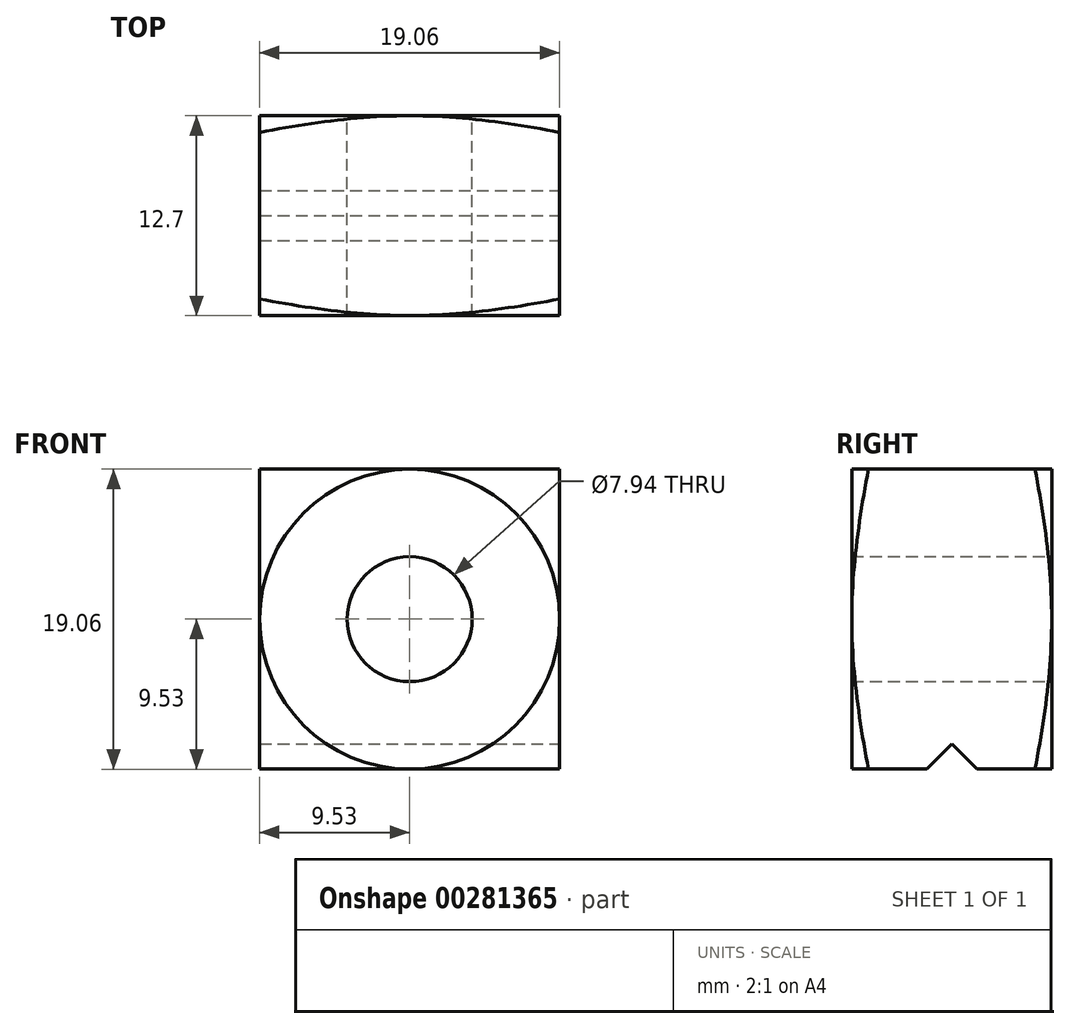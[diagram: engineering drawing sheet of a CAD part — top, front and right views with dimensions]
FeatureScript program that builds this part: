
annotation { "Feature Type Name" : "Feature", "Feature Type Description" : "" }
export const myFeature = defineFeature(function(context is Context, id is Id, definition is map)
    precondition{}
    {
        {
            var Q0;
            Q0=qCreatedBy(makeId("Front.planeOp"),FACE);
            var sketch = newSketch(context, id + "F0", { "sketchPlane" : qUnion([Q0])});
            skLineSegment(sketch, "E0.bottom", {"start": v(-9.52, -9.52) * mm, "end": v(9.52, -9.52) * mm});
            skLineSegment(sketch, "E0.top", {"start": v(-9.53, 9.52) * mm, "end": v(9.53, 9.52) * mm});
            skLineSegment(sketch, "E0.left", {"start": v(-9.53, -9.52) * mm, "end": v(-9.53, 9.52) * mm});
            skLineSegment(sketch, "E0.right", {"start": v(9.53, -9.52) * mm, "end": v(9.53, 9.52) * mm});
            skPoint(sketch, "E0.middle", {"position": v(0, 0) * mm});
            skCircle(sketch, "E1", {"center": v(0, 0) * mm, "radius": 3.97 * mm});
            skCircle(sketch, "E2", {"center": v(0, 0) * mm, "radius": 9.53 * mm});
            skSolve(sketch);
        }
        {
            var Q0;
            Q0=qSketchRegion(id+"F0",true);
            extrude(context, id + "F1", {"entities" : qUnion([Q0]), "depth" : 12.7 * mm});
        }
        {
            var Q0;
            Q0=makeQuery(id+"F1.opExtrude","SWEPT_FACE",FACE,{"disambiguationData":[OSD([sQuery(id+"F0.wireOp",EDGE,"E0.right")])]});
            var sketch = newSketch(context, id + "F2", { "sketchPlane" : qUnion([Q0])});
            skLineSegment(sketch, "E3", {"start": v(-6.35, -7.94) * mm, "end": v(-7.94, -9.52) * mm});
            skPoint(sketch, "E3.startSnap0", {"position": v(-6.35, -9.52) * mm});
            skLineSegment(sketch, "E4", {"start": v(-6.35, -7.94) * mm, "end": v(-4.76, -9.52) * mm});
            skLineSegment(sketch, "E5", {"start": v(-6.35, -7.94) * mm, "end": v(-6.35, -15.34) * mm, "construction": true});
            skSolve(sketch);
        }
        {
            var Q0;
            Q0=qSketchRegion(id+"F2",true);
            var Q1;
            {var subQ0=sQuery(id+"F2.wireOp",EDGE,"E3");Q1=makeQuery(id+"F2.imprint","IMPRINT",FACE,{"disambiguationData":[TD([[makeQuery(id+"F2.imprint","IMPRINT",EDGE,{"derivedFrom":subQ0}),1.0]])]});}
            extrude(context, id + "F3", {"entities" : qUnion([Q0, Q1]), "operationType" : NewBodyOperationType.REMOVE, "oppositeDirection" : true, "depth" : 19.05 * mm});
        }
        {
            var Q0;
            Q0=makeQuery(id+"F1.opExtrude","SWEPT_FACE",FACE,{"disambiguationData":[OSD([sQuery(id+"F0.wireOp",EDGE,"E0.right")])]});
            var Q1;
            Q1=makeQuery(id+"F1.opExtrude","SWEPT_FACE",FACE,{"disambiguationData":[OSD([sQuery(id+"F0.wireOp",EDGE,"E0.left")])]});
            cPlane(context, id + "F4", {"entities" : qUnion([Q0, Q1]), "cplaneType" : CPlaneType.MID_PLANE, "offset" : 25.4 * mm, "width" : 152.4 * mm, "height" : 152.4 * mm});
        }
        {
            var Q0;
            Q0=qCreatedBy(id+"F4.planeOp",FACE);
            var sketch = newSketch(context, id + "F5", { "sketchPlane" : qUnion([Q0])});
            skLineSegment(sketch, "E6.0.0", {"start": v(-7.94, -9.52) * mm, "end": v(-6.35, -7.94) * mm});
            skLineSegment(sketch, "E6.0.1", {"start": v(-6.35, -7.94) * mm, "end": v(-4.76, -9.52) * mm});
            skLineSegment(sketch, "E6.0.2", {"start": v(-4.76, -9.52) * mm, "end": v(0, -9.52) * mm});
            skLineSegment(sketch, "E6.0.3", {"start": v(0, -9.52) * mm, "end": v(0, 9.52) * mm});
            skLineSegment(sketch, "E6.0.4", {"start": v(0, 9.52) * mm, "end": v(-12.7, 9.52) * mm});
            skLineSegment(sketch, "E6.0.5", {"start": v(-12.7, 9.52) * mm, "end": v(-12.7, -9.52) * mm});
            skLineSegment(sketch, "E6.0.6", {"start": v(-12.7, -9.52) * mm, "end": v(-7.94, -9.52) * mm});
            skLineSegment(sketch, "E7", {"start": v(-12.7, 9.52) * mm, "end": v(-12.7, 20.54) * mm});
            skLineSegment(sketch, "E8", {"start": v(-12.7, 20.54) * mm, "end": v(-9.75, 20.54) * mm});
            skLineSegment(sketch, "E9", {"start": v(-9.75, 20.54) * mm, "end": v(-12.7, 9.52) * mm});
            skLineSegment(sketch, "E10", {"start": v(0, 9.52) * mm, "end": v(0, 20.54) * mm});
            skLineSegment(sketch, "E11", {"start": v(0, 20.54) * mm, "end": v(-2.95, 20.54) * mm});
            skLineSegment(sketch, "E12", {"start": v(-2.95, 20.54) * mm, "end": v(0, 9.53) * mm});
            skSolve(sketch);
        }
        {
            var Q0;
            Q0=makeQuery(id+"F5.imprint","IMPRINT",FACE,{"disambiguationData":[TD([[makeQuery(id+"F5.imprint","IMPRINT",EDGE,{"derivedFrom":sQuery(id+"F5.wireOp",EDGE,"E7")}),-1.0]])]});
            var Q1;
            Q1=makeQuery(id+"F5.imprint","IMPRINT",FACE,{"disambiguationData":[TD([[makeQuery(id+"F5.imprint","IMPRINT",EDGE,{"derivedFrom":sQuery(id+"F5.wireOp",EDGE,"E10")}),1.0]])]});
            var Q2;
            Q2=makeQuery(id+"F1.opExtrude","SWEPT_FACE",FACE,{"disambiguationData":[OSD([sQuery(id+"F0.wireOp",EDGE,"E1")])]});
            revolve(context, id + "F6", {"operationType" : NewBodyOperationType.REMOVE, "entities" : qUnion([Q0, Q1]), "axis" : qUnion([Q2]), "revolveType" : RevolveType.FULL, "oppositeDirection" : true});
        }
    });
